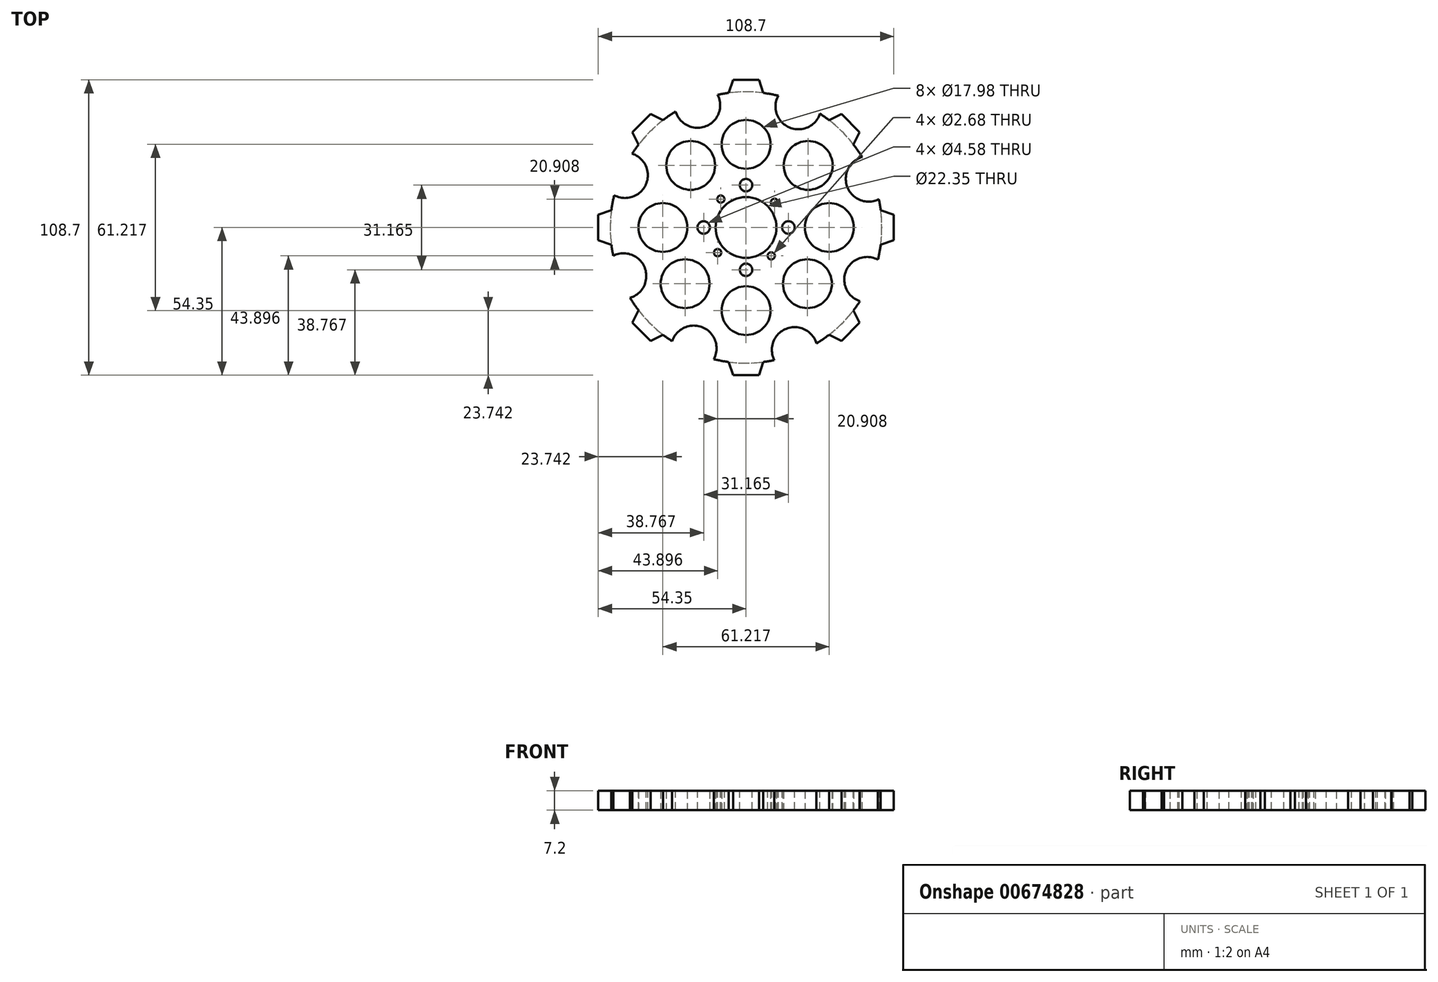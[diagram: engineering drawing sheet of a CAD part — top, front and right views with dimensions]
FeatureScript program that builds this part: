
annotation { "Feature Type Name" : "Feature", "Feature Type Description" : "" }
export const myFeature = defineFeature(function(context is Context, id is Id, definition is map)
    precondition{}
    {
        {
            var Q0;
            Q0=qCreatedBy(makeId("Top.planeOp"),FACE);
            var sketch = newSketch(context, id + "F0", { "sketchPlane" : qUnion([Q0])});
            skCircle(sketch, "E0", {"center": v(0, 0) * mm, "radius": 30.6 * mm});
            skCircle(sketch, "E1", {"center": v(22.85, 22.85) * mm, "radius": 9 * mm});
            skCircle(sketch, "E2", {"center": v(0, 30.6) * mm, "radius": 9 * mm});
            skCircle(sketch, "E3", {"center": v(-20.37, 22.85) * mm, "radius": 9 * mm});
            skCircle(sketch, "E4", {"center": v(-30.6, 0) * mm, "radius": 9 * mm});
            skCircle(sketch, "E5", {"center": v(-22.4, -20.7) * mm, "radius": 9 * mm});
            skCircle(sketch, "E6", {"center": v(0, -30.6) * mm, "radius": 9 * mm});
            skCircle(sketch, "E7", {"center": v(22.57, -20.7) * mm, "radius": 9 * mm});
            skCircle(sketch, "E8", {"center": v(30.6, 0) * mm, "radius": 9 * mm});
            skCircle(sketch, "E9", {"center": v(0, 0) * mm, "radius": 49.94 * mm});
            skCircle(sketch, "E10", {"center": v(0, 0) * mm, "radius": 11.18 * mm});
            skLineSegment(sketch, "E11", {"start": v(0, 0) * mm, "end": v(84.87, 84.87) * mm, "construction": true});
            skLineSegment(sketch, "E12", {"start": v(84.87, 84.87) * mm, "end": v(-88.2, -88.2) * mm, "construction": true});
            skLineSegment(sketch, "E13", {"start": v(0, 0) * mm, "end": v(-79, 88.62) * mm, "construction": true});
            skLineSegment(sketch, "E14", {"start": v(-79, 88.62) * mm, "end": v(82.83, -92.9) * mm, "construction": true});
            skLineSegment(sketch, "E15", {"start": v(0, -58.96) * mm, "end": v(0, 59.86) * mm});
            skLineSegment(sketch, "E16", {"start": v(-66.03, 0) * mm, "end": v(74.2, 0) * mm});
            skSolve(sketch);
        }
        {
            var Q0;
            Q0 = qSketchRegion(id + "F0", true);
            var Q1;
            Q1=makeQuery(id+"F0.imprint","IMPRINT",FACE,{"disambiguationData":[TD([[makeQuery(id+"F0.imprint","IMPRINT",EDGE,{"derivedFrom":sQuery(id+"F0.wireOp",EDGE,"E10")}),-1.0]])]});
            extrude(context, id + "F1", {"entities" : qUnion([Q0, Q1]), "depth" : 7.2 * mm, "offsetDistance" : 25.4 * mm});
        }
        {
            var Q0;
            Q0=makeQuery(id+"F1.opExtrude","CAP_FACE",FACE,{"disambiguationData":[OSD([sQuery(id+"F0.wireOp",EDGE,"E1"),sQuery(id+"F0.wireOp",EDGE,"E2"),sQuery(id+"F0.wireOp",EDGE,"E3"),sQuery(id+"F0.wireOp",EDGE,"E4"),sQuery(id+"F0.wireOp",EDGE,"E5"),sQuery(id+"F0.wireOp",EDGE,"E6"),sQuery(id+"F0.wireOp",EDGE,"E7"),sQuery(id+"F0.wireOp",EDGE,"E8"),sQuery(id+"F0.wireOp",EDGE,"E9"),sQuery(id+"F0.wireOp",EDGE,"E10")])],"isStart":false});
            var sketch = newSketch(context, id + "F2", { "sketchPlane" : qUnion([Q0])});
            skLineSegment(sketch, "E17", {"start": v(0, 49.94) * mm, "end": v(6.34, 49.53) * mm});
            skLineSegment(sketch, "E18", {"start": v(0, 49.94) * mm, "end": v(-6.34, 49.53) * mm});
            skLineSegment(sketch, "E19", {"start": v(-6.34, 49.53) * mm, "end": v(-4.74, 54.35) * mm});
            skLineSegment(sketch, "E20", {"start": v(6.34, 49.53) * mm, "end": v(4.74, 54.35) * mm});
            skLineSegment(sketch, "E21", {"start": v(-4.74, 54.35) * mm, "end": v(4.74, 54.35) * mm});
            skLineSegment(sketch, "E22.1.0", {"start": v(-41.78, 35.08) * mm, "end": v(-35.08, 41.78) * mm});
            skLineSegment(sketch, "E22.1.1", {"start": v(-39.5, 30.54) * mm, "end": v(-41.78, 35.08) * mm});
            skLineSegment(sketch, "E22.1.2", {"start": v(-30.54, 39.5) * mm, "end": v(-35.08, 41.78) * mm});
            skLineSegment(sketch, "E22.2.0", {"start": v(-54.35, -4.74) * mm, "end": v(-54.35, 4.74) * mm});
            skLineSegment(sketch, "E22.2.1", {"start": v(-49.53, -6.34) * mm, "end": v(-54.35, -4.74) * mm});
            skLineSegment(sketch, "E22.2.2", {"start": v(-49.53, 6.34) * mm, "end": v(-54.35, 4.74) * mm});
            skPoint(sketch, "E22.center", {"position": v(0, 0) * mm});
            skLineSegment(sketch, "E23.1.3.0", {"start": v(-35.08, -41.78) * mm, "end": v(-41.78, -35.08) * mm});
            skLineSegment(sketch, "E23.3.3.0", {"start": v(-30.54, -39.5) * mm, "end": v(-35.08, -41.78) * mm});
            skLineSegment(sketch, "E23.6.3.0", {"start": v(-39.5, -30.54) * mm, "end": v(-41.78, -35.08) * mm});
            skLineSegment(sketch, "E23.1.4.0", {"start": v(4.74, -54.35) * mm, "end": v(-4.74, -54.35) * mm});
            skLineSegment(sketch, "E23.3.4.0", {"start": v(6.34, -49.53) * mm, "end": v(4.74, -54.35) * mm});
            skLineSegment(sketch, "E23.6.4.0", {"start": v(-6.34, -49.53) * mm, "end": v(-4.74, -54.35) * mm});
            skLineSegment(sketch, "E23.1.5.0", {"start": v(41.78, -35.08) * mm, "end": v(35.08, -41.78) * mm});
            skLineSegment(sketch, "E23.3.5.0", {"start": v(39.5, -30.54) * mm, "end": v(41.78, -35.08) * mm});
            skLineSegment(sketch, "E23.6.5.0", {"start": v(30.54, -39.5) * mm, "end": v(35.08, -41.78) * mm});
            skLineSegment(sketch, "E23.1.6.0", {"start": v(54.35, 4.74) * mm, "end": v(54.35, -4.74) * mm});
            skLineSegment(sketch, "E23.3.6.0", {"start": v(49.53, 6.34) * mm, "end": v(54.35, 4.74) * mm});
            skLineSegment(sketch, "E23.6.6.0", {"start": v(49.53, -6.34) * mm, "end": v(54.35, -4.74) * mm});
            skLineSegment(sketch, "E23.1.7.0", {"start": v(35.08, 41.78) * mm, "end": v(41.78, 35.08) * mm});
            skLineSegment(sketch, "E23.3.7.0", {"start": v(30.54, 39.5) * mm, "end": v(35.08, 41.78) * mm});
            skLineSegment(sketch, "E23.6.7.0", {"start": v(39.5, 30.54) * mm, "end": v(41.78, 35.08) * mm});
            skArc(sketch, "E24", {"start": v(9.79, 48.97) * mm, "mid": v(15.5, 36.76) * mm, "end": v(28.21, 41.2) * mm});
            skArc(sketch, "E25.1.0", {"start": v(-27.7, 41.54) * mm, "mid": v(-15.04, 36.94) * mm, "end": v(-9.18, 49.08) * mm});
            skArc(sketch, "E25.2.0", {"start": v(-48.97, 9.79) * mm, "mid": v(-36.76, 15.5) * mm, "end": v(-41.2, 28.21) * mm});
            skArc(sketch, "E25.3.0", {"start": v(-41.54, -27.7) * mm, "mid": v(-36.94, -15.04) * mm, "end": v(-49.08, -9.18) * mm});
            skArc(sketch, "E25.4.0", {"start": v(-9.79, -48.97) * mm, "mid": v(-15.5, -36.76) * mm, "end": v(-28.21, -41.2) * mm});
            skArc(sketch, "E25.5.0", {"start": v(27.7, -41.54) * mm, "mid": v(15.04, -36.94) * mm, "end": v(9.18, -49.08) * mm});
            skArc(sketch, "E25.6.0", {"start": v(48.97, -9.79) * mm, "mid": v(36.76, -15.5) * mm, "end": v(41.2, -28.21) * mm});
            skArc(sketch, "E25.7.0", {"start": v(41.54, 27.7) * mm, "mid": v(36.94, 15.04) * mm, "end": v(49.08, 9.18) * mm});
            skSolve(sketch);
        }
        {
            var Q0;
            Q0 = qSketchRegion(id + "F2", true);
            var Q1;
            Q1=makeQuery(id+"F2.imprint","IMPRINT",FACE,{"disambiguationData":[TD([[makeQuery(id+"F2.imprint","IMPRINT",EDGE,{"derivedFrom":sQuery(id+"F2.wireOp",EDGE,"E23.1.7.0")}),-1.0]])]});
            var Q2;
            Q2=makeQuery(id+"F2.imprint","IMPRINT",FACE,{"disambiguationData":[TD([[makeQuery(id+"F2.imprint","IMPRINT",EDGE,{"derivedFrom":sQuery(id+"F2.wireOp",EDGE,"E23.1.6.0")}),-1.0]])]});
            var Q3;
            Q3=makeQuery(id+"F2.imprint","IMPRINT",FACE,{"disambiguationData":[TD([[makeQuery(id+"F2.imprint","IMPRINT",EDGE,{"derivedFrom":sQuery(id+"F2.wireOp",EDGE,"E23.1.5.0")}),-1.0]])]});
            var Q4;
            Q4=makeQuery(id+"F2.imprint","IMPRINT",FACE,{"disambiguationData":[TD([[makeQuery(id+"F2.imprint","IMPRINT",EDGE,{"derivedFrom":sQuery(id+"F2.wireOp",EDGE,"E23.1.4.0")}),-1.0]])]});
            var Q5;
            Q5=makeQuery(id+"F2.imprint","IMPRINT",FACE,{"disambiguationData":[TD([[makeQuery(id+"F2.imprint","IMPRINT",EDGE,{"derivedFrom":sQuery(id+"F2.wireOp",EDGE,"E23.1.3.0")}),-1.0]])]});
            var Q6;
            Q6=makeQuery(id+"F2.imprint","IMPRINT",FACE,{"disambiguationData":[TD([[makeQuery(id+"F2.imprint","IMPRINT",EDGE,{"derivedFrom":sQuery(id+"F2.wireOp",EDGE,"E22.2.0")}),-1.0]])]});
            var Q7;
            Q7=makeQuery(id+"F2.imprint","IMPRINT",FACE,{"disambiguationData":[TD([[makeQuery(id+"F2.imprint","IMPRINT",EDGE,{"derivedFrom":sQuery(id+"F2.wireOp",EDGE,"E22.1.0")}),-1.0]])]});
            extrude(context, id + "F3", {"entities" : qUnion([Q0, Q1, Q2, Q3, Q4, Q5, Q6, Q7]), "operationType" : NewBodyOperationType.ADD, "oppositeDirection" : true, "depth" : 7.2 * mm, "offsetDistance" : 25.4 * mm});
        }
        {
            var Q0;
            {var subQ0=sQuery(id+"F0.wireOp",EDGE,"E9");Q0=makeQuery(id+"F3.boolean.opBoolean","MERGE",FACE,{"derivedFrom":[makeQuery(id+"F1.opExtrude","CAP_FACE",FACE,{"disambiguationData":[OSD([sQuery(id+"F0.wireOp",EDGE,"E1"),sQuery(id+"F0.wireOp",EDGE,"E2"),sQuery(id+"F0.wireOp",EDGE,"E3"),sQuery(id+"F0.wireOp",EDGE,"E4"),sQuery(id+"F0.wireOp",EDGE,"E5"),sQuery(id+"F0.wireOp",EDGE,"E6"),sQuery(id+"F0.wireOp",EDGE,"E7"),sQuery(id+"F0.wireOp",EDGE,"E8"),subQ0,sQuery(id+"F0.wireOp",EDGE,"E10")])],"isStart":false}),makeQuery(id+"F3.opExtrude","CAP_FACE",FACE,{"disambiguationData":[OSD([sQuery(id+"F2.wireOp",EDGE,"E17"),sQuery(id+"F2.wireOp",EDGE,"E18"),sQuery(id+"F2.wireOp",EDGE,"E19"),sQuery(id+"F2.wireOp",EDGE,"E20"),sQuery(id+"F2.wireOp",EDGE,"E21")])],"isStart":true}),makeQuery(id+"F3.opExtrude","CAP_FACE",FACE,{"disambiguationData":[OSD([subQ0,sQuery(id+"F2.wireOp",EDGE,"E22.1.0"),sQuery(id+"F2.wireOp",EDGE,"E22.1.1"),sQuery(id+"F2.wireOp",EDGE,"E22.1.2")])],"isStart":true}),makeQuery(id+"F3.opExtrude","CAP_FACE",FACE,{"disambiguationData":[OSD([subQ0,sQuery(id+"F2.wireOp",EDGE,"E22.2.0"),sQuery(id+"F2.wireOp",EDGE,"E22.2.1"),sQuery(id+"F2.wireOp",EDGE,"E22.2.2")])],"isStart":true}),makeQuery(id+"F3.opExtrude","CAP_FACE",FACE,{"disambiguationData":[OSD([subQ0,sQuery(id+"F2.wireOp",EDGE,"E23.1.3.0"),sQuery(id+"F2.wireOp",EDGE,"E23.3.3.0"),sQuery(id+"F2.wireOp",EDGE,"E23.6.3.0")])],"isStart":true}),makeQuery(id+"F3.opExtrude","CAP_FACE",FACE,{"disambiguationData":[OSD([subQ0,sQuery(id+"F2.wireOp",EDGE,"E23.1.4.0"),sQuery(id+"F2.wireOp",EDGE,"E23.3.4.0"),sQuery(id+"F2.wireOp",EDGE,"E23.6.4.0")])],"isStart":true}),makeQuery(id+"F3.opExtrude","CAP_FACE",FACE,{"disambiguationData":[OSD([subQ0,sQuery(id+"F2.wireOp",EDGE,"E23.1.5.0"),sQuery(id+"F2.wireOp",EDGE,"E23.3.5.0"),sQuery(id+"F2.wireOp",EDGE,"E23.6.5.0")])],"isStart":true}),makeQuery(id+"F3.opExtrude","CAP_FACE",FACE,{"disambiguationData":[OSD([subQ0,sQuery(id+"F2.wireOp",EDGE,"E23.1.6.0"),sQuery(id+"F2.wireOp",EDGE,"E23.3.6.0"),sQuery(id+"F2.wireOp",EDGE,"E23.6.6.0")])],"isStart":true}),makeQuery(id+"F3.opExtrude","CAP_FACE",FACE,{"disambiguationData":[OSD([subQ0,sQuery(id+"F2.wireOp",EDGE,"E23.1.7.0"),sQuery(id+"F2.wireOp",EDGE,"E23.3.7.0"),sQuery(id+"F2.wireOp",EDGE,"E23.6.7.0")])],"isStart":true})]});}
            var sketch = newSketch(context, id + "F4", { "sketchPlane" : qUnion([Q0])});
            skArc(sketch, "E26", {"start": v(11.87, 48.5) * mm, "mid": v(15.9, 36.82) * mm, "end": v(27.18, 41.9) * mm});
            skArc(sketch, "E27.1.0", {"start": v(-25.9, 42.7) * mm, "mid": v(-14.79, 37.28) * mm, "end": v(-10.4, 48.84) * mm});
            skArc(sketch, "E27.2.0", {"start": v(-48.5, 11.87) * mm, "mid": v(-36.82, 15.9) * mm, "end": v(-41.9, 27.18) * mm});
            skArc(sketch, "E27.3.0", {"start": v(-42.7, -25.9) * mm, "mid": v(-37.28, -14.79) * mm, "end": v(-48.84, -10.4) * mm});
            skArc(sketch, "E27.4.0", {"start": v(-11.87, -48.5) * mm, "mid": v(-15.9, -36.82) * mm, "end": v(-27.18, -41.9) * mm});
            skArc(sketch, "E27.5.0", {"start": v(25.9, -42.7) * mm, "mid": v(14.79, -37.28) * mm, "end": v(10.4, -48.84) * mm});
            skArc(sketch, "E27.6.0", {"start": v(48.5, -11.87) * mm, "mid": v(36.82, -15.9) * mm, "end": v(41.9, -27.18) * mm});
            skArc(sketch, "E27.7.0", {"start": v(42.7, 25.9) * mm, "mid": v(37.28, 14.79) * mm, "end": v(48.84, 10.4) * mm});
            skPoint(sketch, "E27.center", {"position": v(0, 0) * mm});
            skCircle(sketch, "E28", {"center": v(0, 15.58) * mm, "radius": 2.29 * mm});
            skCircle(sketch, "E29.1.0", {"center": v(-15.58, 0) * mm, "radius": 2.29 * mm});
            skCircle(sketch, "E29.2.0", {"center": v(0, -15.58) * mm, "radius": 2.29 * mm});
            skCircle(sketch, "E29.3.0", {"center": v(15.58, 0) * mm, "radius": 2.29 * mm});
            skCircle(sketch, "E30", {"center": v(10.45, 9.27) * mm, "radius": 1.34 * mm});
            skCircle(sketch, "E31.1.0", {"center": v(-9.27, 10.45) * mm, "radius": 1.34 * mm});
            skCircle(sketch, "E31.2.0", {"center": v(-10.45, -9.27) * mm, "radius": 1.34 * mm});
            skCircle(sketch, "E31.3.0", {"center": v(9.27, -10.45) * mm, "radius": 1.34 * mm});
            skSolve(sketch);
        }
        {
            var Q0;
            {var subQ0=sQuery(id+"F4.wireOp",EDGE,"E27.1.0");Q0=makeQuery(id+"F4.imprint","IMPRINT",FACE,{"disambiguationData":[TD([[makeQuery(id+"F4.imprint","IMPRINT",EDGE,{"derivedFrom":subQ0}),1.0]])]});}
            var Q1;
            {var subQ0=sQuery(id+"F4.wireOp",EDGE,"E27.2.0");Q1=makeQuery(id+"F4.imprint","IMPRINT",FACE,{"disambiguationData":[TD([[makeQuery(id+"F4.imprint","IMPRINT",EDGE,{"derivedFrom":subQ0}),1.0]])]});}
            var Q2;
            {var subQ0=sQuery(id+"F4.wireOp",EDGE,"E27.4.0");Q2=makeQuery(id+"F4.imprint","IMPRINT",FACE,{"disambiguationData":[TD([[makeQuery(id+"F4.imprint","IMPRINT",EDGE,{"derivedFrom":subQ0}),1.0]])]});}
            var Q3;
            {var subQ0=sQuery(id+"F4.wireOp",EDGE,"E27.3.0");Q3=makeQuery(id+"F4.imprint","IMPRINT",FACE,{"disambiguationData":[TD([[makeQuery(id+"F4.imprint","IMPRINT",EDGE,{"derivedFrom":subQ0}),1.0]])]});}
            var Q4;
            {var subQ0=sQuery(id+"F4.wireOp",EDGE,"E27.5.0");Q4=makeQuery(id+"F4.imprint","IMPRINT",FACE,{"disambiguationData":[TD([[makeQuery(id+"F4.imprint","IMPRINT",EDGE,{"derivedFrom":subQ0}),1.0]])]});}
            var Q5;
            {var subQ0=sQuery(id+"F4.wireOp",EDGE,"E27.6.0");Q5=makeQuery(id+"F4.imprint","IMPRINT",FACE,{"disambiguationData":[TD([[makeQuery(id+"F4.imprint","IMPRINT",EDGE,{"derivedFrom":subQ0}),1.0]])]});}
            var Q6;
            {var subQ0=sQuery(id+"F4.wireOp",EDGE,"E27.7.0");Q6=makeQuery(id+"F4.imprint","IMPRINT",FACE,{"disambiguationData":[TD([[makeQuery(id+"F4.imprint","IMPRINT",EDGE,{"derivedFrom":subQ0}),1.0]])]});}
            var Q7;
            {var subQ0=sQuery(id+"F4.wireOp",EDGE,"E26");Q7=makeQuery(id+"F4.imprint","IMPRINT",FACE,{"disambiguationData":[TD([[makeQuery(id+"F4.imprint","IMPRINT",EDGE,{"derivedFrom":subQ0}),1.0]])]});}
            var Q8;
            Q8=makeQuery(id+"F4.imprint","IMPRINT",FACE,{"disambiguationData":[TD([[makeQuery(id+"F4.imprint","IMPRINT",EDGE,{"derivedFrom":sQuery(id+"F4.wireOp",EDGE,"E29.1.0")}),1.0]])]});
            var Q9;
            Q9=makeQuery(id+"F4.imprint","IMPRINT",FACE,{"disambiguationData":[TD([[makeQuery(id+"F4.imprint","IMPRINT",EDGE,{"derivedFrom":sQuery(id+"F4.wireOp",EDGE,"E31.1.0")}),1.0]])]});
            var Q10;
            Q10=makeQuery(id+"F4.imprint","IMPRINT",FACE,{"disambiguationData":[TD([[makeQuery(id+"F4.imprint","IMPRINT",EDGE,{"derivedFrom":sQuery(id+"F4.wireOp",EDGE,"E28")}),1.0]])]});
            var Q11;
            Q11=makeQuery(id+"F4.imprint","IMPRINT",FACE,{"disambiguationData":[TD([[makeQuery(id+"F4.imprint","IMPRINT",EDGE,{"derivedFrom":sQuery(id+"F4.wireOp",EDGE,"E30")}),1.0]])]});
            var Q12;
            Q12=makeQuery(id+"F4.imprint","IMPRINT",FACE,{"disambiguationData":[TD([[makeQuery(id+"F4.imprint","IMPRINT",EDGE,{"derivedFrom":sQuery(id+"F4.wireOp",EDGE,"E29.3.0")}),1.0]])]});
            var Q13;
            Q13=makeQuery(id+"F4.imprint","IMPRINT",FACE,{"disambiguationData":[TD([[makeQuery(id+"F4.imprint","IMPRINT",EDGE,{"derivedFrom":sQuery(id+"F4.wireOp",EDGE,"E31.3.0")}),1.0]])]});
            var Q14;
            Q14=makeQuery(id+"F4.imprint","IMPRINT",FACE,{"disambiguationData":[TD([[makeQuery(id+"F4.imprint","IMPRINT",EDGE,{"derivedFrom":sQuery(id+"F4.wireOp",EDGE,"E29.2.0")}),1.0]])]});
            var Q15;
            Q15=makeQuery(id+"F4.imprint","IMPRINT",FACE,{"disambiguationData":[TD([[makeQuery(id+"F4.imprint","IMPRINT",EDGE,{"derivedFrom":sQuery(id+"F4.wireOp",EDGE,"E31.2.0")}),1.0]])]});
            extrude(context, id + "F5", {"entities" : qUnion([Q0, Q1, Q2, Q3, Q4, Q5, Q6, Q7, Q8, Q9, Q10, Q11, Q12, Q13, Q14, Q15]), "operationType" : NewBodyOperationType.REMOVE, "endBound" : BoundingType.THROUGH_ALL, "oppositeDirection" : true, "depth" : 7.2 * mm, "offsetDistance" : 25.4 * mm});
        }
    });
